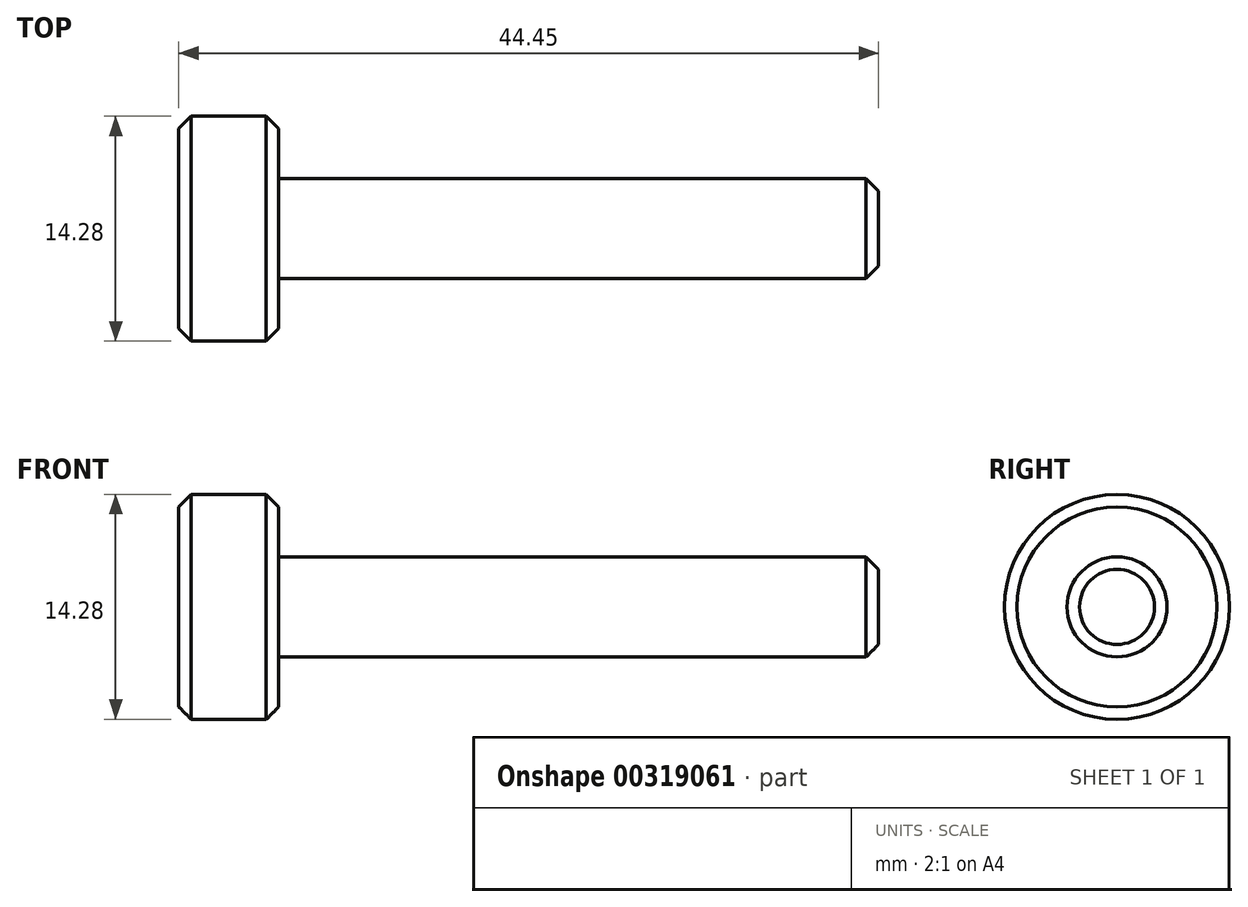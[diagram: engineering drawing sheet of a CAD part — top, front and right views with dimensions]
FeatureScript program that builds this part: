
annotation { "Feature Type Name" : "Feature", "Feature Type Description" : "" }
export const myFeature = defineFeature(function(context is Context, id is Id, definition is map)
    precondition{}
    {
        {
            var Q0;
            Q0=qCreatedBy(makeId("Right.planeOp"),FACE);
            var sketch = newSketch(context, id + "F0", { "sketchPlane" : qUnion([Q0])});
            skCircle(sketch, "E0", {"center": v(0, 0) * mm, "radius": 7.14 * mm});
            skSolve(sketch);
        }
        {
            var Q0;
            Q0 = qSketchRegion(id + "F0", true);
            extrude(context, id + "F1", {"entities" : qUnion([Q0]), "depth" : 6.35 * mm});
        }
        {
            var Q0;
            Q0=makeQuery(id+"F1.opExtrude","CAP_FACE",FACE,{"disambiguationData":[OSD([sQuery(id+"F0.wireOp",EDGE,"E0")])],"isStart":false});
            var sketch = newSketch(context, id + "F2", { "sketchPlane" : qUnion([Q0])});
            skCircle(sketch, "E1", {"center": v(0, 0) * mm, "radius": 3.18 * mm});
            skSolve(sketch);
        }
        {
            var Q0;
            Q0 = qSketchRegion(id + "F2", true);
            extrude(context, id + "F3", {"entities" : qUnion([Q0]), "operationType" : NewBodyOperationType.ADD, "depth" : 38.1 * mm});
        }
        {
            var Q0;
            Q0=makeQuery(id+"F1.opExtrude","CAP_EDGE",EDGE,{"disambiguationData":[OSD([sQuery(id+"F0.wireOp",EDGE,"E0")])],"isStart":false});
            var Q1;
            Q1=makeQuery(id+"F1.opExtrude","CAP_EDGE",EDGE,{"disambiguationData":[OSD([sQuery(id+"F0.wireOp",EDGE,"E0")])],"isStart":true});
            var Q2;
            Q2=makeQuery(id+"F3.opExtrude","CAP_EDGE",EDGE,{"disambiguationData":[OSD([sQuery(id+"F2.wireOp",EDGE,"E1")])],"isStart":false});
            chamfer(context, id + "F4", {"entities" : qUnion([Q0, Q1, Q2]), "width" : 0.8 * mm, "tangentPropagation" : true});
        }
    });
